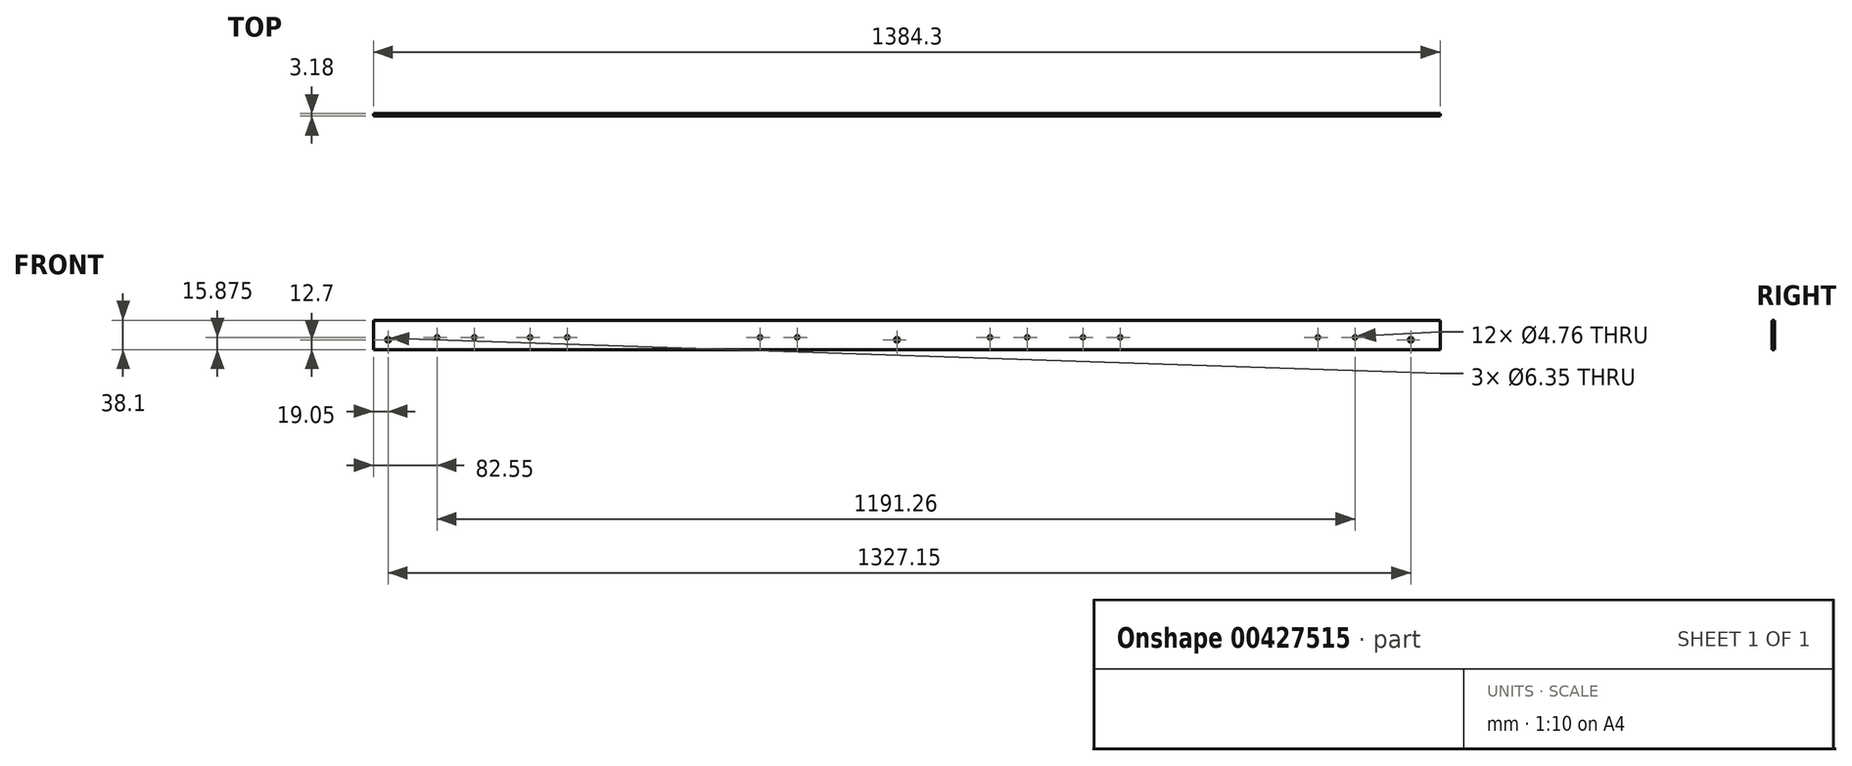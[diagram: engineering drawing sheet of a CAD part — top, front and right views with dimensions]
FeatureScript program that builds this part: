
annotation { "Feature Type Name" : "Feature", "Feature Type Description" : "" }
export const myFeature = defineFeature(function(context is Context, id is Id, definition is map)
    precondition{}
    {
        {
            var Q0;
            Q0=qCreatedBy(makeId("Front.planeOp"),FACE);
            var sketch = newSketch(context, id + "F0", { "sketchPlane" : qUnion([Q0])});
            skLineSegment(sketch, "E0.bottom", {"start": v(0, 0) * mm, "end": v(1384.3, 0) * mm});
            skLineSegment(sketch, "E0.top", {"start": v(0, 38.1) * mm, "end": v(1384.3, 38.1) * mm});
            skLineSegment(sketch, "E0.left", {"start": v(0, 0) * mm, "end": v(0, 38.1) * mm});
            skLineSegment(sketch, "E0.right", {"start": v(1384.3, 0) * mm, "end": v(1384.3, 38.1) * mm});
            skSolve(sketch);
        }
        {
            var Q0;
            Q0=makeQuery(id+"F0.imprint","IMPRINT",FACE,{"disambiguationData":[TD([[makeQuery(id+"F0.imprint","IMPRINT",EDGE,{"derivedFrom":sQuery(id+"F0.wireOp",EDGE,"E0.bottom")}),1.0]])]});
            extrude(context, id + "F1", {"entities" : qUnion([Q0]), "oppositeDirection" : true, "depth" : 3.17 * mm});
        }
        {
            var Q0;
            Q0=makeQuery(id+"F1.opExtrude","CAP_FACE",FACE,{"disambiguationData":[OSD([sQuery(id+"F0.wireOp",EDGE,"E0.bottom"),sQuery(id+"F0.wireOp",EDGE,"E0.top"),sQuery(id+"F0.wireOp",EDGE,"E0.left"),sQuery(id+"F0.wireOp",EDGE,"E0.right")])],"isStart":true});
            var sketch = newSketch(context, id + "F2", { "sketchPlane" : qUnion([Q0])});
            skCircle(sketch, "E1", {"center": v(19.05, 12.7) * mm, "radius": 3.18 * mm});
            skCircle(sketch, "E2", {"center": v(679.45, 12.7) * mm, "radius": 3.18 * mm});
            skCircle(sketch, "E3", {"center": v(1346.2, 12.7) * mm, "radius": 3.18 * mm});
            skSolve(sketch);
        }
        {
            var Q0;
            Q0=makeQuery(id+"F2.imprint","IMPRINT",FACE,{"disambiguationData":[TD([[makeQuery(id+"F2.imprint","IMPRINT",EDGE,{"derivedFrom":sQuery(id+"F2.wireOp",EDGE,"E3")}),1.0]])]});
            var Q1;
            Q1=makeQuery(id+"F2.imprint","IMPRINT",FACE,{"disambiguationData":[TD([[makeQuery(id+"F2.imprint","IMPRINT",EDGE,{"derivedFrom":sQuery(id+"F2.wireOp",EDGE,"E2")}),1.0]])]});
            var Q2;
            Q2=makeQuery(id+"F2.imprint","IMPRINT",FACE,{"disambiguationData":[TD([[makeQuery(id+"F2.imprint","IMPRINT",EDGE,{"derivedFrom":sQuery(id+"F2.wireOp",EDGE,"E1")}),1.0]])]});
            extrude(context, id + "F3", {"entities" : qUnion([Q0, Q1, Q2]), "operationType" : NewBodyOperationType.REMOVE, "endBound" : BoundingType.THROUGH_ALL, "oppositeDirection" : true, "depth" : 25.4 * mm});
        }
        {
            var Q0;
            Q0=makeQuery(id+"F1.opExtrude","CAP_FACE",FACE,{"disambiguationData":[OSD([sQuery(id+"F0.wireOp",EDGE,"E0.bottom"),sQuery(id+"F0.wireOp",EDGE,"E0.top"),sQuery(id+"F0.wireOp",EDGE,"E0.left"),sQuery(id+"F0.wireOp",EDGE,"E0.right")])],"isStart":true});
            var sketch = newSketch(context, id + "F4", { "sketchPlane" : qUnion([Q0])});
            skCircle(sketch, "E4", {"center": v(82.55, 15.88) * mm, "radius": 2.38 * mm});
            skCircle(sketch, "E5.1.0.0", {"center": v(130.8, 15.88) * mm, "radius": 2.38 * mm});
            skLineSegment(sketch, "E5.direction1", {"start": v(82.55, 15.88) * mm, "end": v(130.8, 15.88) * mm, "construction": true});
            skCircle(sketch, "E6", {"center": v(203.2, 15.88) * mm, "radius": 2.38 * mm});
            skCircle(sketch, "E7.1.0.0", {"center": v(251.46, 15.88) * mm, "radius": 2.38 * mm});
            skLineSegment(sketch, "E7.direction1", {"start": v(203.2, 15.88) * mm, "end": v(251.46, 15.88) * mm, "construction": true});
            skCircle(sketch, "E8", {"center": v(501.65, 15.88) * mm, "radius": 2.38 * mm});
            skCircle(sketch, "E9.1.0.0", {"center": v(549.9, 15.88) * mm, "radius": 2.38 * mm});
            skLineSegment(sketch, "E9.direction1", {"start": v(501.65, 15.88) * mm, "end": v(549.9, 15.88) * mm, "construction": true});
            skCircle(sketch, "E10", {"center": v(800.1, 15.88) * mm, "radius": 2.38 * mm});
            skCircle(sketch, "E11.1.0.0", {"center": v(848.36, 15.88) * mm, "radius": 2.38 * mm});
            skLineSegment(sketch, "E11.direction1", {"start": v(800.1, 15.88) * mm, "end": v(848.36, 15.88) * mm, "construction": true});
            skCircle(sketch, "E12", {"center": v(920.75, 15.88) * mm, "radius": 2.38 * mm});
            skCircle(sketch, "E13.1.0.0", {"center": v(969, 15.88) * mm, "radius": 2.38 * mm});
            skLineSegment(sketch, "E13.direction1", {"start": v(920.75, 15.88) * mm, "end": v(969, 15.88) * mm, "construction": true});
            skCircle(sketch, "E14", {"center": v(1225.55, 15.88) * mm, "radius": 2.38 * mm});
            skCircle(sketch, "E15.1.0.0", {"center": v(1273.81, 15.88) * mm, "radius": 2.38 * mm});
            skLineSegment(sketch, "E15.direction1", {"start": v(1225.55, 15.88) * mm, "end": v(1273.81, 15.88) * mm, "construction": true});
            skSolve(sketch);
        }
        {
            var Q0;
            Q0=makeQuery(id+"F4.imprint","IMPRINT",FACE,{"disambiguationData":[TD([[makeQuery(id+"F4.imprint","IMPRINT",EDGE,{"derivedFrom":sQuery(id+"F4.wireOp",EDGE,"E4")}),1.0]])]});
            var Q1;
            Q1=makeQuery(id+"F4.imprint","IMPRINT",FACE,{"disambiguationData":[TD([[makeQuery(id+"F4.imprint","IMPRINT",EDGE,{"derivedFrom":sQuery(id+"F4.wireOp",EDGE,"E5.1.0.0")}),1.0]])]});
            var Q2;
            Q2=makeQuery(id+"F4.imprint","IMPRINT",FACE,{"disambiguationData":[TD([[makeQuery(id+"F4.imprint","IMPRINT",EDGE,{"derivedFrom":sQuery(id+"F4.wireOp",EDGE,"E6")}),1.0]])]});
            var Q3;
            Q3=makeQuery(id+"F4.imprint","IMPRINT",FACE,{"disambiguationData":[TD([[makeQuery(id+"F4.imprint","IMPRINT",EDGE,{"derivedFrom":sQuery(id+"F4.wireOp",EDGE,"E7.1.0.0")}),1.0]])]});
            var Q4;
            Q4=makeQuery(id+"F4.imprint","IMPRINT",FACE,{"disambiguationData":[TD([[makeQuery(id+"F4.imprint","IMPRINT",EDGE,{"derivedFrom":sQuery(id+"F4.wireOp",EDGE,"E8")}),1.0]])]});
            var Q5;
            Q5=makeQuery(id+"F4.imprint","IMPRINT",FACE,{"disambiguationData":[TD([[makeQuery(id+"F4.imprint","IMPRINT",EDGE,{"derivedFrom":sQuery(id+"F4.wireOp",EDGE,"E9.1.0.0")}),1.0]])]});
            var Q6;
            Q6=makeQuery(id+"F4.imprint","IMPRINT",FACE,{"disambiguationData":[TD([[makeQuery(id+"F4.imprint","IMPRINT",EDGE,{"derivedFrom":sQuery(id+"F4.wireOp",EDGE,"E12")}),1.0]])]});
            var Q7;
            Q7=makeQuery(id+"F4.imprint","IMPRINT",FACE,{"disambiguationData":[TD([[makeQuery(id+"F4.imprint","IMPRINT",EDGE,{"derivedFrom":sQuery(id+"F4.wireOp",EDGE,"E13.1.0.0")}),1.0]])]});
            var Q8;
            Q8=makeQuery(id+"F4.imprint","IMPRINT",FACE,{"disambiguationData":[TD([[makeQuery(id+"F4.imprint","IMPRINT",EDGE,{"derivedFrom":sQuery(id+"F4.wireOp",EDGE,"E14")}),1.0]])]});
            var Q9;
            Q9=makeQuery(id+"F4.imprint","IMPRINT",FACE,{"disambiguationData":[TD([[makeQuery(id+"F4.imprint","IMPRINT",EDGE,{"derivedFrom":sQuery(id+"F4.wireOp",EDGE,"E15.1.0.0")}),1.0]])]});
            var Q10;
            Q10=makeQuery(id+"F4.imprint","IMPRINT",FACE,{"disambiguationData":[TD([[makeQuery(id+"F4.imprint","IMPRINT",EDGE,{"derivedFrom":sQuery(id+"F4.wireOp",EDGE,"E10")}),1.0]])]});
            var Q11;
            Q11=makeQuery(id+"F4.imprint","IMPRINT",FACE,{"disambiguationData":[TD([[makeQuery(id+"F4.imprint","IMPRINT",EDGE,{"derivedFrom":sQuery(id+"F4.wireOp",EDGE,"E11.1.0.0")}),1.0]])]});
            extrude(context, id + "F5", {"entities" : qUnion([Q0, Q1, Q2, Q3, Q4, Q5, Q6, Q7, Q8, Q9, Q10, Q11]), "operationType" : NewBodyOperationType.REMOVE, "endBound" : BoundingType.THROUGH_ALL, "oppositeDirection" : true, "depth" : 25.4 * mm});
        }
    });
